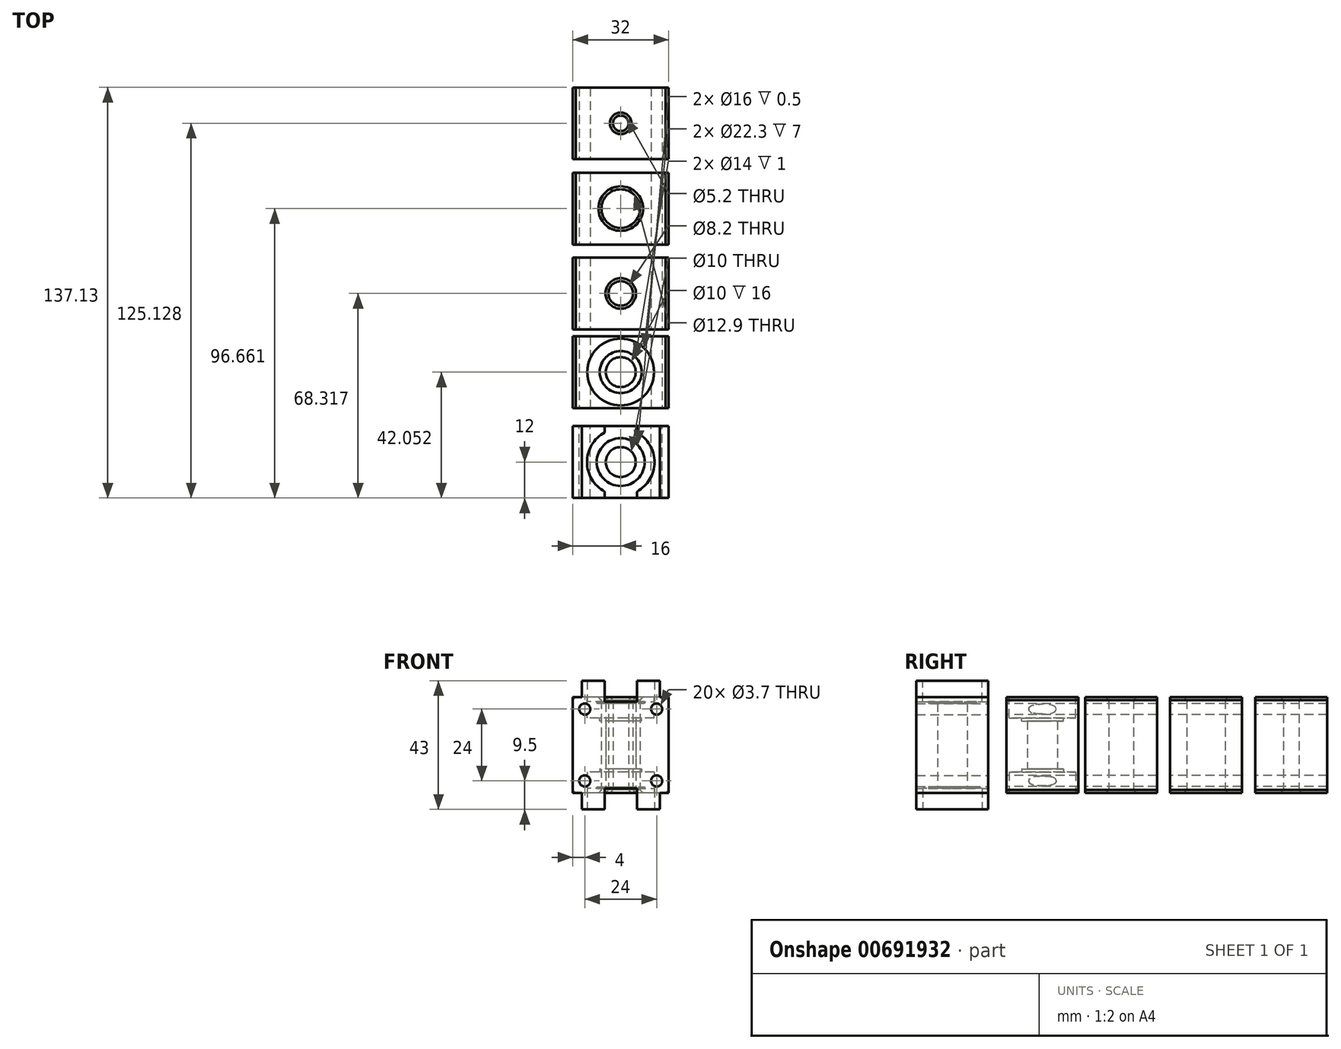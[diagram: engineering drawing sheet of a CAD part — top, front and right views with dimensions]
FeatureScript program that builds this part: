
annotation { "Feature Type Name" : "Feature", "Feature Type Description" : "" }
export const myFeature = defineFeature(function(context is Context, id is Id, definition is map)
    precondition{}
    {
        {
            var Q0;
            Q0=qCreatedBy(makeId("Top.planeOp"),FACE);
            var sketch = newSketch(context, id + "F0", { "sketchPlane" : qUnion([Q0])});
            skLineSegment(sketch, "E0.bottom", {"start": v(16, 18.05) * mm, "end": v(-16, 18.05) * mm});
            skLineSegment(sketch, "E0.top", {"start": v(16, 42.05) * mm, "end": v(-16, 42.05) * mm});
            skLineSegment(sketch, "E0.left", {"start": v(16, 18.05) * mm, "end": v(16, 42.05) * mm});
            skLineSegment(sketch, "E0.right", {"start": v(-16, 18.05) * mm, "end": v(-16, 42.05) * mm});
            skPoint(sketch, "E0.middle", {"position": v(0, 30.05) * mm});
            skCircle(sketch, "E1", {"center": v(0, 30.05) * mm, "radius": 11.15 * mm});
            skCircle(sketch, "E2", {"center": v(0, 30.05) * mm, "radius": 5 * mm});
            skLineSegment(sketch, "E3.bottom", {"start": v(16, 44.32) * mm, "end": v(-16, 44.32) * mm});
            skLineSegment(sketch, "E3.top", {"start": v(16, 68.32) * mm, "end": v(-16, 68.32) * mm});
            skLineSegment(sketch, "E3.left", {"start": v(16, 44.32) * mm, "end": v(16, 68.32) * mm});
            skLineSegment(sketch, "E3.right", {"start": v(-16, 44.32) * mm, "end": v(-16, 68.32) * mm});
            skPoint(sketch, "E3.middle", {"position": v(0, 56.32) * mm});
            skCircle(sketch, "E4", {"center": v(0, 56.32) * mm, "radius": 4.1 * mm});
            skLineSegment(sketch, "E5.bottom", {"start": v(16, 72.66) * mm, "end": v(-16, 72.66) * mm});
            skLineSegment(sketch, "E5.top", {"start": v(16, 96.66) * mm, "end": v(-16, 96.66) * mm});
            skLineSegment(sketch, "E5.left", {"start": v(16, 72.66) * mm, "end": v(16, 96.66) * mm});
            skLineSegment(sketch, "E5.right", {"start": v(-16, 72.66) * mm, "end": v(-16, 96.66) * mm});
            skPoint(sketch, "E5.middle", {"position": v(0, 84.66) * mm});
            skCircle(sketch, "E6", {"center": v(0, 84.66) * mm, "radius": 6.45 * mm});
            skLineSegment(sketch, "E7.bottom", {"start": v(16, 101.13) * mm, "end": v(-16, 101.13) * mm});
            skLineSegment(sketch, "E7.top", {"start": v(16, 125.13) * mm, "end": v(-16, 125.13) * mm});
            skLineSegment(sketch, "E7.left", {"start": v(16, 101.13) * mm, "end": v(16, 125.13) * mm});
            skLineSegment(sketch, "E7.right", {"start": v(-16, 101.13) * mm, "end": v(-16, 125.13) * mm});
            skPoint(sketch, "E7.middle", {"position": v(0, 113.13) * mm});
            skCircle(sketch, "E8", {"center": v(0, 113.13) * mm, "radius": 2.6 * mm});
            skCircle(sketch, "E9", {"center": v(0, 30.05) * mm, "radius": 7 * mm});
            skSolve(sketch);
        }
        {
            var Q0;
            Q0 = qSketchRegion(id + "F0", true);
            var Q1;
            Q1=makeQuery(id+"F0.imprint","IMPRINT",FACE,{"disambiguationData":[TD([[makeQuery(id+"F0.imprint","IMPRINT",EDGE,{"derivedFrom":sQuery(id+"F0.wireOp",EDGE,"E1")}),1.0]])]});
            var Q2;
            Q2=makeQuery(id+"F0.imprint","IMPRINT",FACE,{"disambiguationData":[TD([[makeQuery(id+"F0.imprint","IMPRINT",EDGE,{"derivedFrom":sQuery(id+"F0.wireOp",EDGE,"E2")}),-1.0]])]});
            extrude(context, id + "F1", {"entities" : qUnion([Q0, Q1, Q2]), "depth" : 32 * mm, "offsetDistance" : 25 * mm});
        }
        {
            var Q0;
            Q0=qCreatedBy(makeId("Front.planeOp"),FACE);
            var sketch = newSketch(context, id + "F2", { "sketchPlane" : qUnion([Q0])});
            skLineSegment(sketch, "E10", {"start": v(-21.02, 28) * mm, "end": v(25.37, 28) * mm, "construction": true});
            skLineSegment(sketch, "E11", {"start": v(21.76, 4) * mm, "end": v(-22, 4) * mm, "construction": true});
            skLineSegment(sketch, "E12", {"start": v(-12, 3.79) * mm, "end": v(-12, 18.47) * mm, "construction": true});
            skLineSegment(sketch, "E13", {"start": v(12, 4.03) * mm, "end": v(12, 29.77) * mm, "construction": true});
            skCircle(sketch, "E14", {"center": v(-12, 28) * mm, "radius": 1.85 * mm});
            skCircle(sketch, "E15", {"center": v(12, 28) * mm, "radius": 1.85 * mm});
            skCircle(sketch, "E16", {"center": v(12, 4) * mm, "radius": 1.85 * mm});
            skCircle(sketch, "E17", {"center": v(-12, 4) * mm, "radius": 1.85 * mm});
            skSolve(sketch);
        }
        {
            var Q0;
            Q0 = qSketchRegion(id + "F2", true);
            extrude(context, id + "F3", {"entities" : qUnion([Q0]), "operationType" : NewBodyOperationType.REMOVE, "endBound" : BoundingType.THROUGH_ALL, "oppositeDirection" : true, "depth" : 25 * mm, "offsetDistance" : 25 * mm});
        }
        {
            var Q0;
            Q0=makeQuery(id+"F1.opExtrude","CAP_FACE",FACE,{"disambiguationData":[OSD([sQuery(id+"F0.wireOp",EDGE,"E0.bottom"),sQuery(id+"F0.wireOp",EDGE,"E0.top"),sQuery(id+"F0.wireOp",EDGE,"E0.left"),sQuery(id+"F0.wireOp",EDGE,"E0.right"),sQuery(id+"F0.wireOp",EDGE,"E2")])],"isStart":false});
            var sketch = newSketch(context, id + "F4", { "sketchPlane" : qUnion([Q0])});
            skCircle(sketch, "E18.0", {"center": v(0, 30.05) * mm, "radius": 11.15 * mm});
            skCircle(sketch, "E19.0", {"center": v(0, 30.05) * mm, "radius": 7 * mm});
            skSolve(sketch);
        }
        {
            var Q0;
            Q0 = qSketchRegion(id + "F4", true);
            extrude(context, id + "F5", {"entities" : qUnion([Q0]), "operationType" : NewBodyOperationType.REMOVE, "oppositeDirection" : true, "depth" : 7 * mm, "offsetDistance" : 25 * mm});
        }
        {
            var Q0;
            Q0=makeQuery(id+"F0.imprint","IMPRINT",FACE,{"disambiguationData":[TD([[makeQuery(id+"F0.imprint","IMPRINT",EDGE,{"derivedFrom":sQuery(id+"F0.wireOp",EDGE,"E1")}),1.0]])]});
            extrude(context, id + "F6", {"entities" : qUnion([Q0]), "operationType" : NewBodyOperationType.REMOVE, "depth" : 7 * mm, "offsetDistance" : 25 * mm});
        }
        {
            var Q0;
            Q0=makeQuery(id+"F1.opExtrude","CAP_EDGE",EDGE,{"disambiguationData":[OSD([sQuery(id+"F0.wireOp",EDGE,"E8")])],"isStart":false});
            var Q1;
            Q1=makeQuery(id+"F1.opExtrude","CAP_EDGE",EDGE,{"disambiguationData":[OSD([sQuery(id+"F0.wireOp",EDGE,"E6")])],"isStart":false});
            var Q2;
            Q2=makeQuery(id+"F1.opExtrude","CAP_EDGE",EDGE,{"disambiguationData":[OSD([sQuery(id+"F0.wireOp",EDGE,"E4")])],"isStart":false});
            var Q3;
            Q3=makeQuery(id+"F5.boolean.opBoolean","COPY",EDGE,{"derivedFrom":makeQuery(id+"F5.opExtrude","CAP_EDGE",EDGE,{"disambiguationData":[OSD([sQuery(id+"F4.wireOp",EDGE,"E18.0")])],"isStart":true})});
            var Q4;
            Q4=makeQuery(id+"F1.opExtrude","CAP_EDGE",EDGE,{"disambiguationData":[OSD([sQuery(id+"F0.wireOp",EDGE,"E0.left")])],"isStart":false});
            var Q5;
            Q5=makeQuery(id+"F1.opExtrude","CAP_EDGE",EDGE,{"disambiguationData":[OSD([sQuery(id+"F0.wireOp",EDGE,"E3.left")])],"isStart":false});
            var Q6;
            Q6=makeQuery(id+"F1.opExtrude","CAP_EDGE",EDGE,{"disambiguationData":[OSD([sQuery(id+"F0.wireOp",EDGE,"E5.left")])],"isStart":false});
            var Q7;
            Q7=makeQuery(id+"F1.opExtrude","CAP_EDGE",EDGE,{"disambiguationData":[OSD([sQuery(id+"F0.wireOp",EDGE,"E7.left")])],"isStart":false});
            var Q8;
            Q8=makeQuery(id+"F1.opExtrude","CAP_EDGE",EDGE,{"disambiguationData":[OSD([sQuery(id+"F0.wireOp",EDGE,"E0.right")])],"isStart":false});
            var Q9;
            Q9=makeQuery(id+"F1.opExtrude","CAP_EDGE",EDGE,{"disambiguationData":[OSD([sQuery(id+"F0.wireOp",EDGE,"E3.right")])],"isStart":false});
            var Q10;
            Q10=makeQuery(id+"F1.opExtrude","CAP_EDGE",EDGE,{"disambiguationData":[OSD([sQuery(id+"F0.wireOp",EDGE,"E5.right")])],"isStart":false});
            var Q11;
            Q11=makeQuery(id+"F1.opExtrude","CAP_EDGE",EDGE,{"disambiguationData":[OSD([sQuery(id+"F0.wireOp",EDGE,"E7.right")])],"isStart":false});
            var Q12;
            Q12=makeQuery(id+"F6.boolean.opBoolean","COPY",EDGE,{"derivedFrom":makeQuery(id+"F6.opExtrude","CAP_EDGE",EDGE,{"disambiguationData":[OSD([sQuery(id+"F0.wireOp",EDGE,"E1")])],"isStart":true})});
            var Q13;
            Q13=makeQuery(id+"F1.opExtrude","CAP_EDGE",EDGE,{"disambiguationData":[OSD([sQuery(id+"F0.wireOp",EDGE,"E4")])],"isStart":true});
            var Q14;
            Q14=makeQuery(id+"F1.opExtrude","CAP_EDGE",EDGE,{"disambiguationData":[OSD([sQuery(id+"F0.wireOp",EDGE,"E8")])],"isStart":true});
            var Q15;
            Q15=makeQuery(id+"F1.opExtrude","CAP_EDGE",EDGE,{"disambiguationData":[OSD([sQuery(id+"F0.wireOp",EDGE,"E6")])],"isStart":true});
            var Q16;
            Q16=makeQuery(id+"F1.opExtrude","CAP_EDGE",EDGE,{"disambiguationData":[OSD([sQuery(id+"F0.wireOp",EDGE,"E5.left")])],"isStart":true});
            var Q17;
            Q17=makeQuery(id+"F1.opExtrude","CAP_EDGE",EDGE,{"disambiguationData":[OSD([sQuery(id+"F0.wireOp",EDGE,"E3.left")])],"isStart":true});
            var Q18;
            Q18=makeQuery(id+"F1.opExtrude","CAP_EDGE",EDGE,{"disambiguationData":[OSD([sQuery(id+"F0.wireOp",EDGE,"E0.left")])],"isStart":true});
            var Q19;
            Q19=makeQuery(id+"F1.opExtrude","CAP_EDGE",EDGE,{"disambiguationData":[OSD([sQuery(id+"F0.wireOp",EDGE,"E7.left")])],"isStart":true});
            var Q20;
            Q20=makeQuery(id+"F1.opExtrude","CAP_EDGE",EDGE,{"disambiguationData":[OSD([sQuery(id+"F0.wireOp",EDGE,"E7.right")])],"isStart":true});
            var Q21;
            Q21=makeQuery(id+"F1.opExtrude","CAP_EDGE",EDGE,{"disambiguationData":[OSD([sQuery(id+"F0.wireOp",EDGE,"E5.right")])],"isStart":true});
            var Q22;
            Q22=makeQuery(id+"F1.opExtrude","CAP_EDGE",EDGE,{"disambiguationData":[OSD([sQuery(id+"F0.wireOp",EDGE,"E3.right")])],"isStart":true});
            var Q23;
            Q23=makeQuery(id+"F1.opExtrude","CAP_EDGE",EDGE,{"disambiguationData":[OSD([sQuery(id+"F0.wireOp",EDGE,"E0.right")])],"isStart":true});
            chamfer(context, id + "F7", {"entities" : qUnion([Q0, Q1, Q2, Q3, Q4, Q5, Q6, Q7, Q8, Q9, Q10, Q11, Q12, Q13, Q14, Q15, Q16, Q17, Q18, Q19, Q20, Q21, Q22, Q23]), "width" : 1 * mm, "tangentPropagation" : true});
        }
        {
            var Q0;
            Q0=makeQuery(id+"F0.imprint","IMPRINT",FACE,{"disambiguationData":[TD([[makeQuery(id+"F0.imprint","IMPRINT",EDGE,{"derivedFrom":sQuery(id+"F0.wireOp",EDGE,"E2")}),-1.0]])]});
            extrude(context, id + "F8", {"entities" : qUnion([Q0]), "operationType" : NewBodyOperationType.REMOVE, "depth" : 8 * mm, "offsetDistance" : 25 * mm});
        }
        {
            var Q0;
            {var subQ0=sQuery(id+"F0.wireOp",EDGE,"E2");Q0=makeQuery(id+"F5.boolean.opBoolean","SPLIT",FACE,{"disambiguationData":[TD([makeQuery(id+"F1.opExtrude","SWEPT_FACE",FACE,{"disambiguationData":[OSD([subQ0])]})])],"derivedFrom":makeQuery(id+"F1.opExtrude","CAP_FACE",FACE,{"disambiguationData":[OSD([sQuery(id+"F0.wireOp",EDGE,"E0.bottom"),sQuery(id+"F0.wireOp",EDGE,"E0.top"),sQuery(id+"F0.wireOp",EDGE,"E0.left"),sQuery(id+"F0.wireOp",EDGE,"E0.right"),subQ0])],"isStart":false})});}
            extrude(context, id + "F9", {"entities" : qUnion([Q0]), "operationType" : NewBodyOperationType.REMOVE, "oppositeDirection" : true, "depth" : 8 * mm, "offsetDistance" : 25 * mm});
        }
        {
            var Q0;
            Q0=qCreatedBy(makeId("Front.planeOp"),FACE);
            var sketch = newSketch(context, id + "F10", { "sketchPlane" : qUnion([Q0])});
            skLineSegment(sketch, "E20.bottom", {"start": v(-16, 0) * mm, "end": v(-13, 0) * mm});
            skLineSegment(sketch, "E20.top", {"start": v(-16, 32) * mm, "end": v(-13, 32) * mm});
            skLineSegment(sketch, "E20.left", {"start": v(-16, 0) * mm, "end": v(-16, 32) * mm});
            skLineSegment(sketch, "E20.right", {"start": v(16, 0) * mm, "end": v(16, 32) * mm});
            skLineSegment(sketch, "E21.top", {"start": v(-13, 37.5) * mm, "end": v(13, 37.5) * mm});
            skLineSegment(sketch, "E21.left", {"start": v(-13, 32) * mm, "end": v(-13, 37.5) * mm});
            skLineSegment(sketch, "E21.right", {"start": v(13, 32) * mm, "end": v(13, 37.5) * mm});
            skLineSegment(sketch, "E22.top", {"start": v(-13, -5.5) * mm, "end": v(13, -5.5) * mm});
            skLineSegment(sketch, "E22.left", {"start": v(-13, 0) * mm, "end": v(-13, -5.5) * mm});
            skLineSegment(sketch, "E22.right", {"start": v(13, 0) * mm, "end": v(13, -5.5) * mm});
            skLineSegment(sketch, "E23.trimOffspring", {"start": v(13, 32) * mm, "end": v(16, 32) * mm});
            skLineSegment(sketch, "E24.trimOffspring", {"start": v(13, 0) * mm, "end": v(16, 0) * mm});
            skLineSegment(sketch, "E25", {"start": v(11.25, 37.5) * mm, "end": v(11.25, 30.5) * mm});
            skLineSegment(sketch, "E26", {"start": v(11.25, 30.5) * mm, "end": v(8, 30.5) * mm});
            skLineSegment(sketch, "E27", {"start": v(8, 30.5) * mm, "end": v(8, 30) * mm});
            skLineSegment(sketch, "E28", {"start": v(8, 30) * mm, "end": v(5, 30) * mm});
            skLineSegment(sketch, "E29", {"start": v(5, 30) * mm, "end": v(5, 2) * mm});
            skLineSegment(sketch, "E30", {"start": v(5, 2) * mm, "end": v(8, 2) * mm});
            skLineSegment(sketch, "E31", {"start": v(8, 2) * mm, "end": v(8, 1.5) * mm});
            skLineSegment(sketch, "E32", {"start": v(8, 1.5) * mm, "end": v(11.25, 1.5) * mm});
            skLineSegment(sketch, "E33", {"start": v(11.25, 1.5) * mm, "end": v(11.25, -5.5) * mm});
            skLineSegment(sketch, "E34", {"start": v(0, 37.5) * mm, "end": v(0, -5.5) * mm});
            skCircle(sketch, "E35.0", {"center": v(-12, 28) * mm, "radius": 1.85 * mm});
            skCircle(sketch, "E36.0", {"center": v(12, 28) * mm, "radius": 1.85 * mm});
            skCircle(sketch, "E37.0", {"center": v(12, 4) * mm, "radius": 1.85 * mm});
            skCircle(sketch, "E38.0", {"center": v(-12, 4) * mm, "radius": 1.85 * mm});
            skSolve(sketch);
        }
        {
            var Q0;
            Q0=makeQuery(id+"F10.imprint","IMPRINT",FACE,{"disambiguationData":[TD([[makeQuery(id+"F10.imprint","IMPRINT",EDGE,{"derivedFrom":sQuery(id+"F10.wireOp",EDGE,"E20.bottom")}),1.0]])]});
            var Q1;
            {var subQ3=sQuery(id+"F10.wireOp",EDGE,"E25");Q1=makeQuery(id+"F10.imprint","IMPRINT",FACE,{"disambiguationData":[TD([[makeQuery(id+"F10.imprint","IMPRINT",EDGE,{"derivedFrom":subQ3}),-1.0]])]});}
            var Q2;
            Q2=makeQuery(id+"F10.imprint","IMPRINT",FACE,{"disambiguationData":[TD([[makeQuery(id+"F10.imprint","IMPRINT",EDGE,{"derivedFrom":sQuery(id+"F10.wireOp",EDGE,"E20.right")}),1.0]])]});
            extrude(context, id + "F11", {"entities" : qUnion([Q0, Q1, Q2]), "endBound" : BoundingType.SYMMETRIC, "depth" : 24 * mm, "offsetDistance" : 25 * mm});
        }
        {
            var Q0;
            {var subQ3=sQuery(id+"F10.wireOp",EDGE,"E25");Q0=makeQuery(id+"F10.imprint","IMPRINT",FACE,{"disambiguationData":[TD([[makeQuery(id+"F10.imprint","IMPRINT",EDGE,{"derivedFrom":subQ3}),-1.0]])]});}
            var Q1;
            Q1=sQuery(id+"F10.wireOp",EDGE,"E34");
            revolve(context, id + "F12", {"operationType" : NewBodyOperationType.REMOVE, "surfaceOperationType" : NewSurfaceOperationType.NEW, "entities" : qUnion([Q0]), "axis" : qUnion([Q1]), "revolveType" : RevolveType.FULL, "oppositeDirection" : true});
        }
        {
            var Q0;
            Q0=makeQuery(id+"F11.opExtrude","SWEPT_FACE",FACE,{"disambiguationData":[OSD([sQuery(id+"F10.wireOp",EDGE,"E21.top")])]});
            var sketch = newSketch(context, id + "F13", { "sketchPlane" : qUnion([Q0])});
            skLineSegment(sketch, "E39.bottom", {"start": v(5.38, -13.3) * mm, "end": v(-5.38, -13.3) * mm});
            skLineSegment(sketch, "E39.top", {"start": v(5.38, 13.3) * mm, "end": v(-5.38, 13.3) * mm});
            skLineSegment(sketch, "E39.left", {"start": v(5.38, -13.3) * mm, "end": v(5.38, 13.3) * mm});
            skLineSegment(sketch, "E39.right", {"start": v(-5.38, -13.3) * mm, "end": v(-5.38, 13.3) * mm});
            skPoint(sketch, "E39.middle", {"position": v(0, 0) * mm});
            skSolve(sketch);
        }
        {
            var Q0;
            {var subQ0=sQuery(id+"F13.wireOp",EDGE,"E39.left");var subQ1=sQuery(id+"F10.wireOp",EDGE,"E21.top");var subQ2=makeQuery(id+"F11.opExtrude","CAP_EDGE",EDGE,{"disambiguationData":[OSD([subQ1])],"isStart":true});var subQ3=makeQuery(id+"F13.imprint","INTERSECT",VERTEX,{"derivedFrom":[subQ2,subQ0]});Q0=makeQuery(id+"F13.imprint","IMPRINT",FACE,{"disambiguationData":[TD([[makeQuery(id+"F13.imprint","IMPRINT",EDGE,{"disambiguationData":[TD([[subQ3,1.0]])],"derivedFrom":subQ2}),-1.0]])]});}
            var Q1;
            {var subQ0=sQuery(id+"F13.wireOp",EDGE,"E39.left");var subQ1=sQuery(id+"F10.wireOp",EDGE,"E21.top");var subQ2=makeQuery(id+"F11.opExtrude","CAP_EDGE",EDGE,{"disambiguationData":[OSD([subQ1])],"isStart":false});var subQ3=makeQuery(id+"F13.imprint","INTERSECT",VERTEX,{"derivedFrom":[subQ2,subQ0]});Q1=makeQuery(id+"F13.imprint","IMPRINT",FACE,{"disambiguationData":[TD([[makeQuery(id+"F13.imprint","IMPRINT",EDGE,{"disambiguationData":[TD([[subQ3,1.0]])],"derivedFrom":subQ2}),1.0]])]});}
            extrude(context, id + "F14", {"entities" : qUnion([Q0, Q1]), "operationType" : NewBodyOperationType.REMOVE, "oppositeDirection" : true, "depth" : 7 * mm, "offsetDistance" : 25 * mm});
        }
        {
            var Q0;
            Q0=makeQuery(id+"F11.opExtrude","SWEPT_FACE",FACE,{"disambiguationData":[OSD([sQuery(id+"F10.wireOp",EDGE,"E22.top")])]});
            var sketch = newSketch(context, id + "F15", { "sketchPlane" : qUnion([Q0])});
            skPoint(sketch, "E40.0", {"position": v(5.38, 13.3) * mm});
            skPoint(sketch, "E41.0", {"position": v(-5.38, 13.3) * mm});
            skPoint(sketch, "E42.0", {"position": v(5.38, -13.3) * mm});
            skPoint(sketch, "E43.0", {"position": v(-5.38, -13.3) * mm});
            skLineSegment(sketch, "E44.0", {"start": v(-5.38, 13.3) * mm, "end": v(-5.38, -13.3) * mm});
            skLineSegment(sketch, "E45.0", {"start": v(5.38, -13.3) * mm, "end": v(-5.38, -13.3) * mm});
            skLineSegment(sketch, "E46.0", {"start": v(5.38, 13.3) * mm, "end": v(5.38, -13.3) * mm});
            skLineSegment(sketch, "E47.0", {"start": v(5.38, 13.3) * mm, "end": v(-5.38, 13.3) * mm});
            skSolve(sketch);
        }
        {
            var Q0;
            Q0 = qSketchRegion(id + "F15", true);
            extrude(context, id + "F16", {"entities" : qUnion([Q0]), "operationType" : NewBodyOperationType.REMOVE, "oppositeDirection" : true, "depth" : 7 * mm, "offsetDistance" : 25 * mm});
        }
    });
